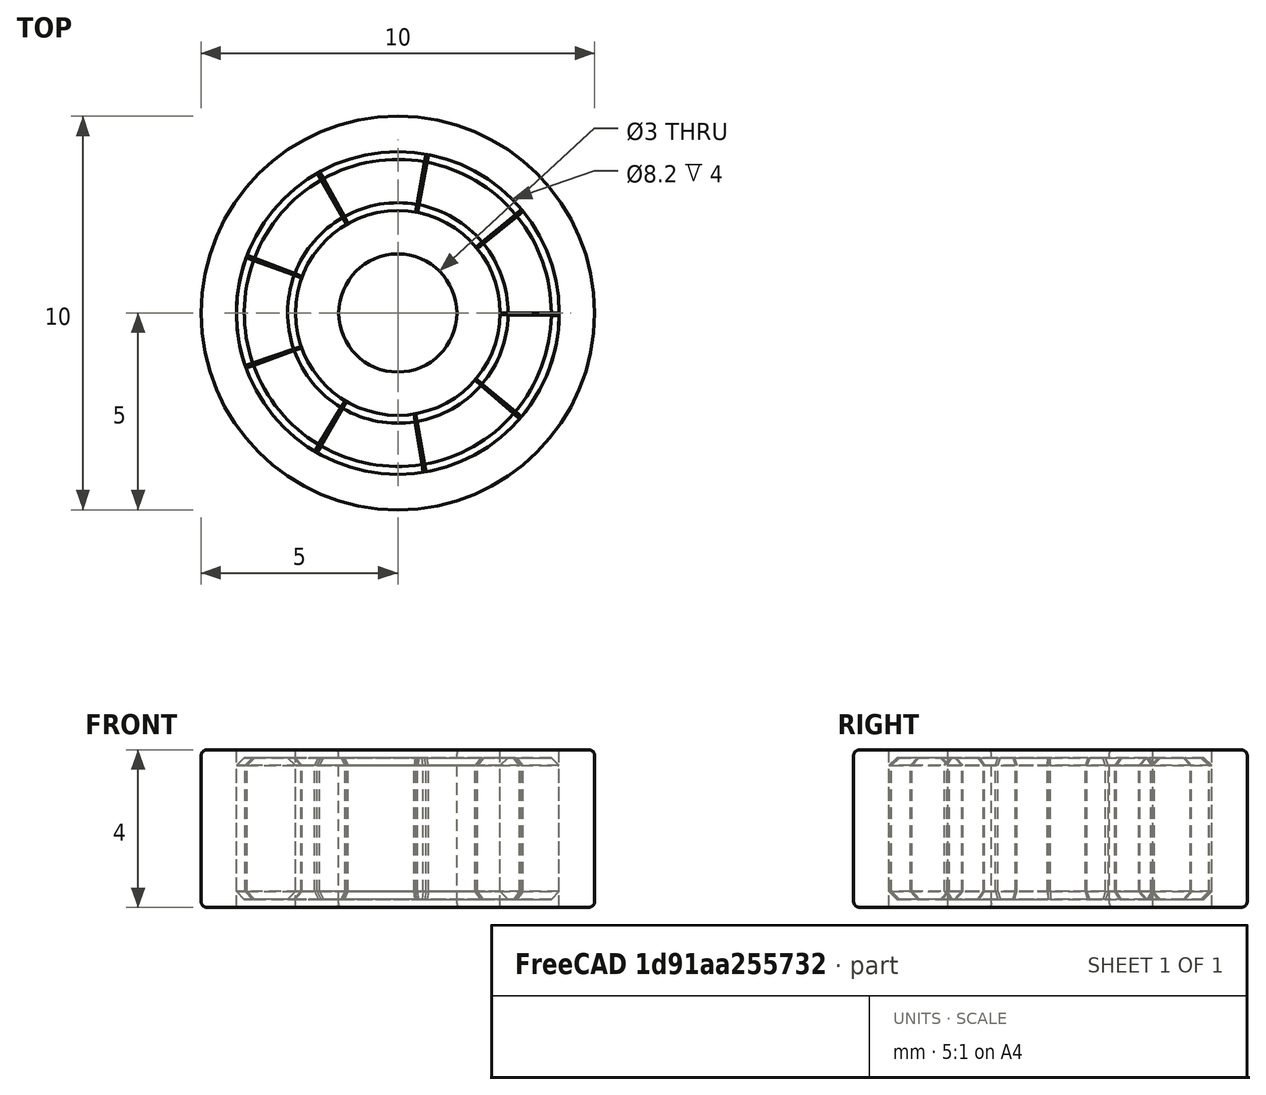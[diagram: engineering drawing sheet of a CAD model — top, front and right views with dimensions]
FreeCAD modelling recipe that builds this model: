
FCSTD DOCUMENT  (FreeCAD 0.17R9175 (Git))
Label: Parametric_Ball_Bearing
License: All rights reserved
LicenseURL: http://de.wikipedia.org/wiki/Alle_Rechte_vorbehalten
objects: Part::Cylinder×6, Part::Cut×3, PartDesign::Fillet×2, Part::Chamfer×1, Part::FeaturePython×1, Part::MultiFuse×1, Spreadsheet::Sheet×1, Part::Compound×1
note: 15 computed .brp shape members not serialized (recipe doc carries the construction recipe); baked Part::Feature solids carry a one-line shape summary decoded from their .brp

FEATURE [Part::Cylinder] Cylinder  label="Exterior"
  Angle = 360
  AttacherType = Attacher::AttachEngine3D
  Height = 4
  Radius = 5
  expr: Height = Spreadsheet.Bt
  expr: Radius = Spreadsheet.De / 2
FEATURE [Part::Cylinder] Cylinder001  label="Interior"
  Angle = 360
  AttacherType = Attacher::AttachEngine3D
  Height = 4
  Radius = 1.5
  expr: Radius = Spreadsheet.di / 2
  expr: Height = Spreadsheet.Bt
FEATURE [Part::Cylinder] Cylinder002  label="Cilindro"
  Angle = 360
  AttacherType = Attacher::AttachEngine3D
  Height = 4
  Radius = 4.1
  expr: Height = Spreadsheet.Bt
  expr: Radius = Spreadsheet.Dm2 / 2
FEATURE [Part::Cut] Cut  label="ExtRing"
  Base = -> Cylinder
  Tool = -> Cylinder002
FEATURE [Part::Cylinder] Cylinder003  label="Cilindro001"
  Angle = 360
  AttacherType = Attacher::AttachEngine3D
  Height = 4
  Radius = 2.6
  expr: Height = Spreadsheet.Bt
  expr: Radius = Spreadsheet.Dm1 / 2
FEATURE [Part::Cut] Cut001  label="Interior001"
  Base = -> Cylinder003
  Tool = -> Cylinder001
FEATURE [Part::Cylinder] Cylinder004  label="Cilindro002"
  Angle = 39
  AttacherType = Attacher::AttachEngine3D
  Height = 3.6
  Placement = pos=(0,0,0.2) rot=(0,0,1;0rad)
  Radius = 4.1
  expr: Radius = Spreadsheet.Dm2 / 2
  expr: Height = Spreadsheet.Bt - 0.4
FEATURE [Part::Cylinder] Cylinder005  label="Cilindro003"
  Angle = 39
  AttacherType = Attacher::AttachEngine3D
  Height = 3.6
  Placement = pos=(0,0,0.2) rot=(0,0,1;0rad)
  Radius = 2.6
  expr: Height = Spreadsheet.Bt - 0.4
  expr: Radius = Spreadsheet.Dm1 / 2
FEATURE [Part::Cut] Cut002
  Base = -> Cylinder004
  Tool = -> Cylinder005
FEATURE [Part::Chamfer] Chamfer001
  Base = -> Cut002
  Edges = 4 edges r=0.2: [Edge1,Edge3,Edge6,Edge11]
FEATURE [Part::FeaturePython] Array  # Draft array (typed FeaturePython)
  Angle = 360
  ArrayType = 1
  Axis = (0,0,1)
  Base = -> Chamfer001
  Center = (0,0,0)
  IntervalX = (1,0,0)
  IntervalY = (0,1,0)
  IntervalZ = (0,0,1)
  NumberPolar = 9
  NumberX = 2
  NumberY = 2
  NumberZ = 1
FEATURE [Part::MultiFuse] Fusion  label="MidRingMetal"
  Shapes = -> [Array]
FEATURE [Spreadsheet::Sheet] Spreadsheet
  cells = B1=Principal Dimensions; C2=D; D2(De)=10; C3=d; D3(di)=3; C4=B; D4(Bt)=4; B5=Secondary Dimensions; C6=d1/d2; D6(Dm1)=5.2; C7=D2/da; D7(Dm2)=8.199999999999999; C8=r1,2; D8(rchamfer)=0.15; C9=ra; D9(ra)=0.1
FEATURE [PartDesign::Fillet] Fillet
  Base = -> Cut001 [Edge5,Edge4]
  Radius = 0.1
  expr: Radius = Spreadsheet.ra
FEATURE [PartDesign::Fillet] Fillet001
  Base = -> Cut [Edge3,Edge1]
  Radius = 0.15
  expr: Radius = Spreadsheet.rchamfer
FEATURE [Part::Compound] Compound  label="Parametric_Ball_Bearing"
  Links = -> [Fillet,Fusion,Fillet001]
